# Revit family: Basin-Wall-Caroma Sunstone 900 Twin1
name_source: partatom
category: Plumbing Fixtures
revit_build: Autodesk Revit 2014 (Build: 20130308_1515(x64)
units: mm (PartAtom-declared; Revit-internal decimal feet)

## types (1)
- Sunstone 900 Twin - 0 Tap Holes
    1 Taphole = No
    3 Tapholes = No
    Assembly Code = D2010310
    CW Connection = No
    Capacity_ANZRS = 3.8 L
    Default Elevation = 865 mm  [stored 2.83793 ft]
    Description = Caroma Sunstone 900 Twin Wall Basin
    HW Connection = No
    Height_ANZRS = 100 mm  [stored 0.328084 ft]
    Length_ANZRS = 900 mm  [stored 2.95276 ft]
    Manufacturer = GWA Bathrooms & Kitchens
    Material_ANZRS = Porcelain-White-Caroma
    Model = 897700
    ModifiedIssue_ANZRS = 20150203.01 $
    Spout Penetration = 100 mm  [stored 0.328084 ft]
    Tap Penetrations = 100 mm  [stored 0.328084 ft]
    Type Comments = White Only, Overflow not available, Sunstone Solid Surface Basin Pop-up Waste supplied
    URL = http://www.specify.caroma.com.au
    Vent Connection = No
    WFU = 1
    Waste = Porcelain-White-Caroma
    Waste Connection = Yes
    WasteOutlet_ANZRS = 0
    Width_ANZRS = 400 mm  [stored 1.31234 ft]

note: [stored X ft] marks values corroborated as IEEE doubles in the binary element streams (Revit-internal decimal feet)

## geometry (parser evidence)
native form markers: Blend x12, Sweep x1
no freeform markers — native parametric forms only
